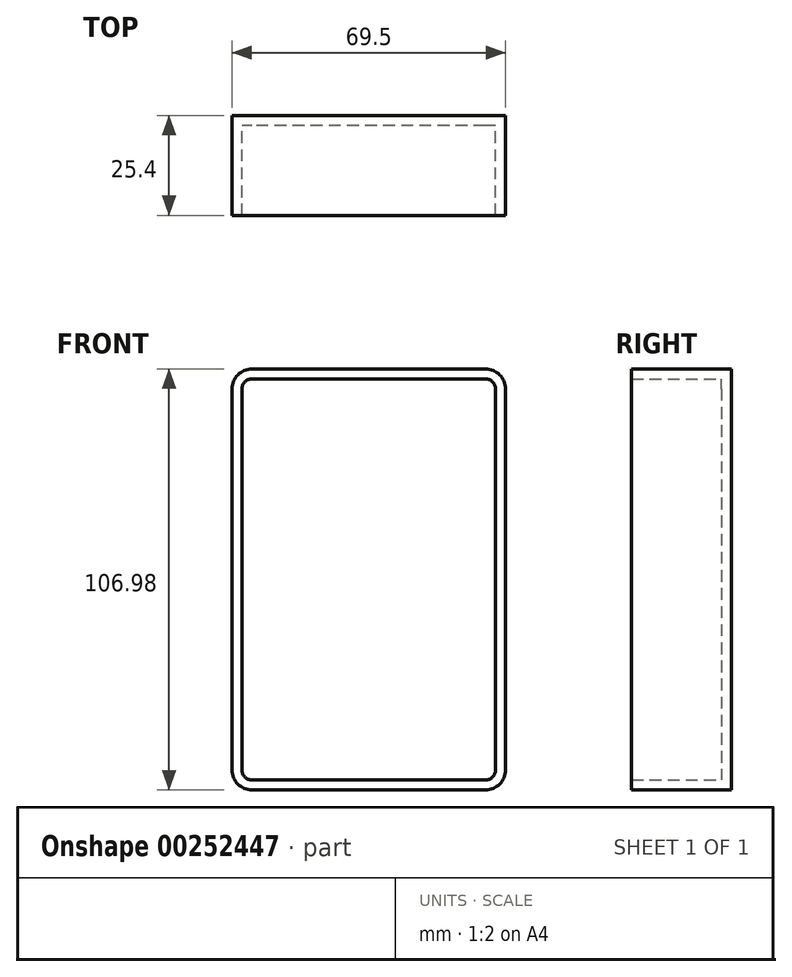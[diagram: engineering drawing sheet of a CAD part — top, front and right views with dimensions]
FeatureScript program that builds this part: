
annotation { "Feature Type Name" : "Feature", "Feature Type Description" : "" }
export const myFeature = defineFeature(function(context is Context, id is Id, definition is map)
    precondition{}
    {
        {
            var Q0;
            Q0=qCreatedBy(makeId("Front.planeOp"),FACE);
            var sketch = newSketch(context, id + "F0", { "sketchPlane" : qUnion([Q0])});
            skLineSegment(sketch, "E0.bottom", {"start": v(34.75, 53.5) * mm, "end": v(-34.75, 53.5) * mm});
            skLineSegment(sketch, "E0.top", {"start": v(34.75, -53.5) * mm, "end": v(-34.75, -53.5) * mm});
            skLineSegment(sketch, "E0.left", {"start": v(34.75, 53.5) * mm, "end": v(34.75, -53.5) * mm});
            skLineSegment(sketch, "E0.right", {"start": v(-34.75, 53.5) * mm, "end": v(-34.75, -53.5) * mm});
            skPoint(sketch, "E0.middle", {"position": v(0, 0) * mm});
            skSolve(sketch);
        }
        {
            var Q0;
            Q0 = qSketchRegion(id + "F0", true);
            extrude(context, id + "F1", {"entities" : qUnion([Q0]), "depth" : 25.4 * mm});
        }
        {
            var Q0;
            Q0=makeQuery(id+"F1.opExtrude","SWEPT_EDGE",EDGE,{"disambiguationData":[OSD([sQuery(id+"F0.wireOp",EDGE,"E0.bottom"),sQuery(id+"F0.wireOp",EDGE,"E0.right")])]});
            var Q1;
            Q1=makeQuery(id+"F1.opExtrude","SWEPT_EDGE",EDGE,{"disambiguationData":[OSD([sQuery(id+"F0.wireOp",EDGE,"E0.top"),sQuery(id+"F0.wireOp",EDGE,"E0.right")])]});
            var Q2;
            Q2=makeQuery(id+"F1.opExtrude","SWEPT_EDGE",EDGE,{"disambiguationData":[OSD([sQuery(id+"F0.wireOp",EDGE,"E0.bottom"),sQuery(id+"F0.wireOp",EDGE,"E0.left")])]});
            var Q3;
            Q3=makeQuery(id+"F1.opExtrude","SWEPT_EDGE",EDGE,{"disambiguationData":[OSD([sQuery(id+"F0.wireOp",EDGE,"E0.top"),sQuery(id+"F0.wireOp",EDGE,"E0.left")])]});
            fillet(context, id + "F2", {"entities" : qUnion([Q0, Q1, Q2, Q3]), "radius" : 5.08 * mm, "tangentPropagation" : true, "allowEdgeOverflow" : false});
        }
        {
            var Q0;
            Q0=makeQuery(id+"F1.opExtrude","CAP_FACE",FACE,{"disambiguationData":[OSD([sQuery(id+"F0.wireOp",EDGE,"E0.bottom"),sQuery(id+"F0.wireOp",EDGE,"E0.top"),sQuery(id+"F0.wireOp",EDGE,"E0.left"),sQuery(id+"F0.wireOp",EDGE,"E0.right")])],"isStart":false});
            shell(context, id + "F3", {"entities" : qUnion([Q0]), "thickness" : 2.54 * mm});
        }
    });
